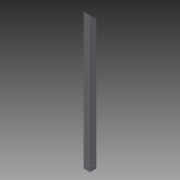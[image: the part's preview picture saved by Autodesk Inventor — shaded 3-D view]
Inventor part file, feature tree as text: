
AUTODESK INVENTOR PART (.ipt)
format: ipt  version: 2013 (Build 170138000, 138)  size: 91,136 bytes
history: native  units: in
note: dims shown in document units (in); Inventor stores cm internally (conversion verified against a paired STEP export)
features: extrude x3, sketch x3
ambient origin geometry x8: Origin, YZ Plane, XZ Plane, XY Plane, X Axis, Y Axis, Z Axis, Center Point
bodies: Solid1 (feature_tree)
feature tree (6):
  extrude  "Extrusion1"  Depth=1.0in
  extrude  "Extrusion2"  Depth=0.75in
  extrude  "Extrusion3"  TaperAngle=45.0deg  [1 undecoded]
  sketch  "Sketch1"  dims[d0=1.0in d1=1.0in]
  sketch  "Sketch2"  dims[d2=0.75in d3=0.75in]
  sketch  "Sketch3"  dims[d4=21.0in d5=0.0in d6=45.0deg d7=1.0in d8=0.0in d9=0.701in d10=0.2in d11=1.0in d12=0.0in]
note: 1 required parameter value undecoded (feature->parameter linkage not recoverable at this tier; creation-order binding heuristic only, values carry confidence <= 0.55)
